# Revit family: 1FHM-C2_TWA-A_RFA
name_source: partatom
category: Pipe Accessories
units: mm (PartAtom-declared; Revit-internal decimal feet)

## family parameters
Always vertical = Yes
Cut with Voids When Loaded = No
OmniClass Number = 23.65.55.14.17
OmniClass Title = Adjusting/Controlling Valves for Liquid Services
Part Type = Normal
Round Connector Dimension = Use Diameter
Shared = No
Work Plane-Based = No

## types (1)
- FHM_C2_088U0092
    088H3106 = TWA-A_RFA : TWA-A_230V_NC/S_0.95m_088H3106
    088H3112 = TWA-A_RFA : TWA-A_230V_NC_0.95m_088H3112
    088H3113 = TWA-A_RFA : TWA-A_230V_NO_0.95m_088H3113
    088H3118 = TWA-A_RFA : TWA-A_230V_NC_5m_088H3118
    088H3119 = TWA-A_RFA : TWA-A_230V_NC_10m_088H3119
    Actuator Type = TWA-A_RFA : TWA-A_24V_NC_0.95m_088H3110
    Description = Supply Temperature Control
    H = 367 mm
    IfcExportAs = IfcValveType
    IfcExportType = FHM
    L = 176 mm
    LOD 200 = No
    LOD 350 = Yes
    Manufacturer = Danfoss
    Max Differential Pressure = 0.6 bar
    Max Operating Pressure = 10 bar
    Max Working Temperature = 90 °C
    Model = 088U0092
    Model Type = FHM_C2_Mixing shunt
    Power = 2 VA
    Power Supply = 230 V AC
    URL = https://store.danfoss.com
    Valve Body Material = Danfoss Brass
    Voltage = 24 V
    W = 88 mm  [stored 0.288714 ft]
    Weight = 3.83 kg

note: [stored X ft] marks values corroborated as IEEE doubles in the binary element streams (Revit-internal decimal feet)

## geometry (parser evidence)
native form markers: Blend x2, Sweep x10
no freeform markers — native parametric forms only
